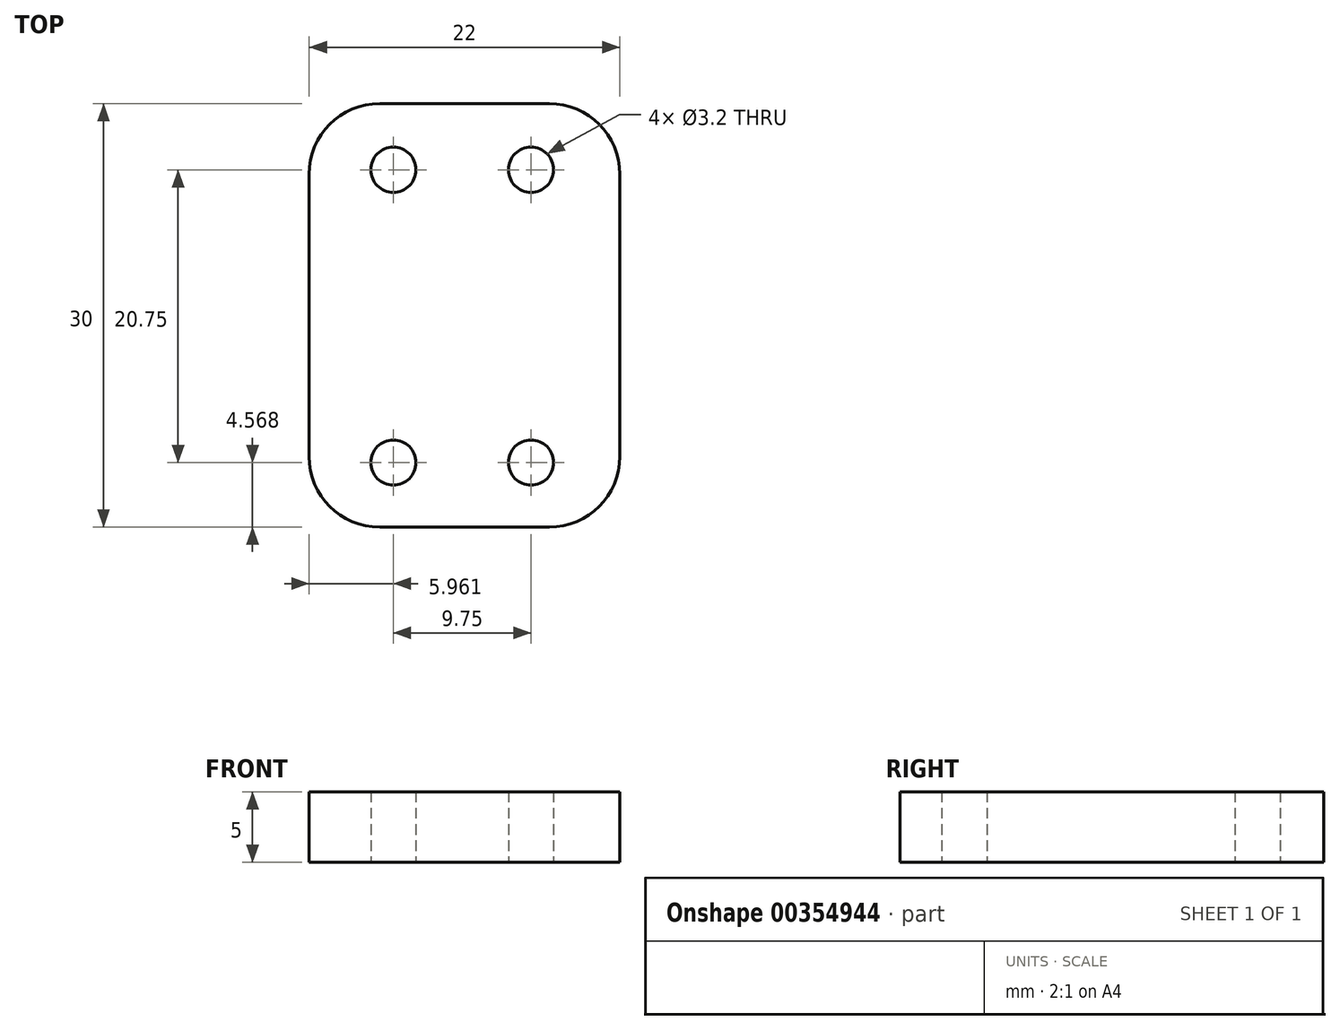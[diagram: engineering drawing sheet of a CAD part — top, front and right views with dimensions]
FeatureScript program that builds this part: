
annotation { "Feature Type Name" : "Feature", "Feature Type Description" : "" }
export const myFeature = defineFeature(function(context is Context, id is Id, definition is map)
    precondition{}
    {
        {
            var Q0;
            Q0=qCreatedBy(makeId("Top.planeOp"),FACE);
            var sketch = newSketch(context, id + "F0", { "sketchPlane" : qUnion([Q0])});
            skLineSegment(sketch, "E0.bottom", {"start": v(-2.8, 0) * mm, "end": v(-24.8, 0) * mm});
            skLineSegment(sketch, "E0.top", {"start": v(-2.8, 30) * mm, "end": v(-24.8, 30) * mm});
            skLineSegment(sketch, "E0.left", {"start": v(-2.8, 0) * mm, "end": v(-2.8, 30) * mm});
            skLineSegment(sketch, "E0.right", {"start": v(-24.8, 0) * mm, "end": v(-24.8, 30) * mm});
            skCircle(sketch, "E1", {"center": v(-18.83, 25.32) * mm, "radius": 1.6 * mm});
            skCircle(sketch, "E2", {"center": v(-18.83, 4.57) * mm, "radius": 1.6 * mm});
            skCircle(sketch, "E3", {"center": v(-9.08, 25.32) * mm, "radius": 1.6 * mm});
            skCircle(sketch, "E4", {"center": v(-9.08, 4.57) * mm, "radius": 1.6 * mm});
            skSolve(sketch);
        }
        {
            var Q0;
            Q0 = qSketchRegion(id + "F0", true);
            extrude(context, id + "F1", {"entities" : qUnion([Q0]), "depth" : 5 * mm});
        }
        {
            var Q0;
            Q0=makeQuery(id+"F1.opExtrude","SWEPT_EDGE",EDGE,{"disambiguationData":[OSD([sQuery(id+"F0.wireOp",EDGE,"E0.top"),sQuery(id+"F0.wireOp",EDGE,"E0.right")])]});
            var Q1;
            Q1=makeQuery(id+"F1.opExtrude","SWEPT_EDGE",EDGE,{"disambiguationData":[OSD([sQuery(id+"F0.wireOp",EDGE,"E0.bottom"),sQuery(id+"F0.wireOp",EDGE,"E0.right")])]});
            var Q2;
            Q2=makeQuery(id+"F1.opExtrude","SWEPT_EDGE",EDGE,{"disambiguationData":[OSD([sQuery(id+"F0.wireOp",EDGE,"E0.bottom"),sQuery(id+"F0.wireOp",EDGE,"E0.left")])]});
            var Q3;
            Q3=makeQuery(id+"F1.opExtrude","SWEPT_EDGE",EDGE,{"disambiguationData":[OSD([sQuery(id+"F0.wireOp",EDGE,"E0.top"),sQuery(id+"F0.wireOp",EDGE,"E0.left")])]});
            fillet(context, id + "F2", {"entities" : qUnion([Q0, Q1, Q2, Q3]), "radius" : 5 * mm, "tangentPropagation" : true, "allowEdgeOverflow" : false});
        }
    });
